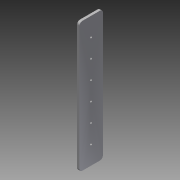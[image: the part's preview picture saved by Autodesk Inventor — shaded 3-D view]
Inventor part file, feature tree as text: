
AUTODESK INVENTOR PART (.ipt)
format: ipt  version: 2014 (Build 180170000, 170)  size: 93,696 bytes
history: native  units: in
note: dims shown in document units (in); Inventor stores cm internally (conversion verified against a paired STEP export)
features: sketch x2, extrude x1, hole x1
ambient origin geometry x8: Origin, YZ Plane, XZ Plane, XY Plane, X Axis, Y Axis, Z Axis, Center Point
bodies: Solid1 (feature_tree)
feature tree (4):
  extrude  "Extrusion1"  Depth=5.5118in
  hole  "Hole2"  [1 undecoded]
  sketch  "Sketch1"  dims[d0=1.0in d1=5.5118in]
  sketch  "Sketch3"  dims[d2=0.125in d3=0.1in d4=0.0in d29=0.7874in d30=2.3622in d32=0.7874in d33=0.3937in d35=1.0in d37=0.0787in d38=0.75in d39=0.375in d40=0.25in d41=0.5635in d42=1.0in d43=0.8108in]
note: 1 required parameter value undecoded (feature->parameter linkage not recoverable at this tier; creation-order binding heuristic only, values carry confidence <= 0.55)
